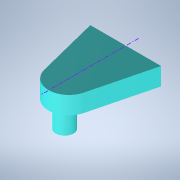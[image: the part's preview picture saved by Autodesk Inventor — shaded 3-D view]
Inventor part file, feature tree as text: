
AUTODESK INVENTOR PART (.ipt)
format: ipt  version: 2022 (Build 260153000, 153)  size: 102,912 bytes
history: imported  units: in
note: dims shown in document units (in); Inventor stores cm internally (conversion verified against a paired STEP export)
features: sketch x1, imported_body x1
ambient origin geometry x8: Origin, YZ Plane, XZ Plane, XY Plane, X Axis, Y Axis, Z Axis, Center Point
bodies: Solid1 (imported_parasolid), Body1 (imported_parasolid)
feature tree (2):
  sketch  "Sketch1"
  imported_body  NMx_Import_Brep_tag  [imported B-rep: ~8 faces, bbox_mm=[60.0, 35.0, 52.384414]]
